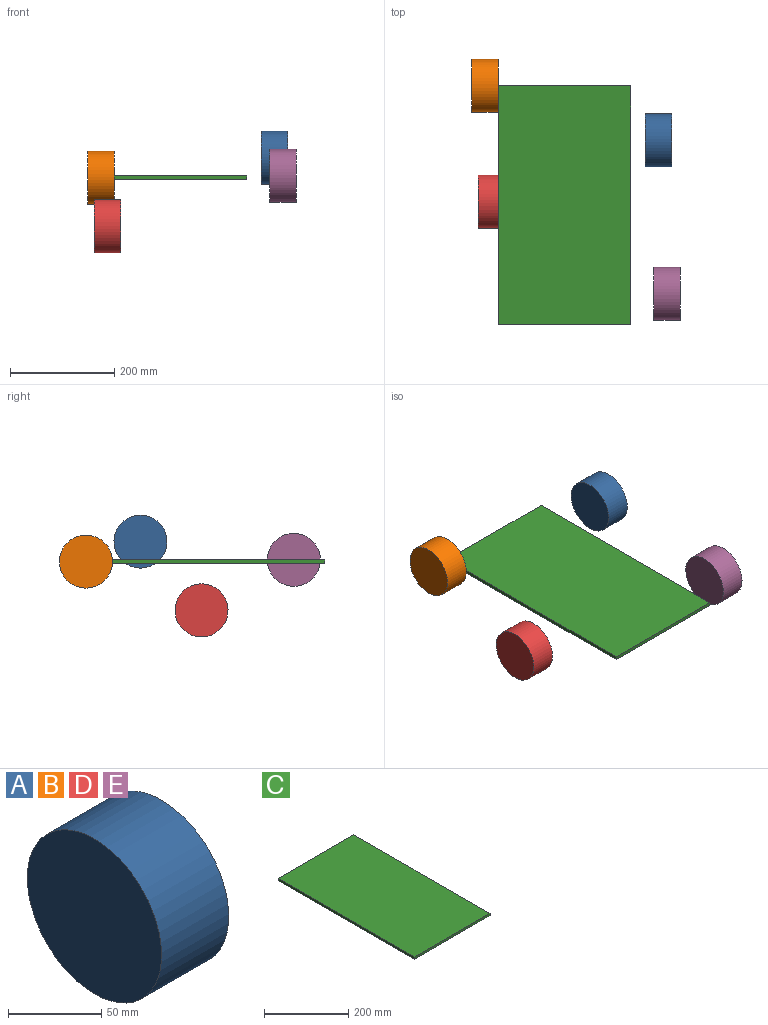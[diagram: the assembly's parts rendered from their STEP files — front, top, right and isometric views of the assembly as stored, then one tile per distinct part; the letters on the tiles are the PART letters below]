
ASSEMBLY  parts=5 mates=1
PART A: 3 faces, bbox 50.8x101.6x101.6 mm
  f0: cylinder r=50.8mm len=101.6mm, axis (-1,0,0), area 16214.6mm2, adj f1,f2
  f1: plane 101.6x101.6mm, normal (1,0,0), area 8107.3mm2, adj f0
  f2: plane 101.6x101.6mm, normal (-1,0,0), area 8107.3mm2, adj f0
PART B: same geometry as A
PART C: 6 faces, bbox 254x457.2x6.4 mm
  f0: plane 254x6.35mm, normal (0,-1,0), area 1612.9mm2, adj f1,f3,f4,f5
  f1: plane 457.2x6.35mm, normal (1,0,0), area 2903.2mm2, adj f0,f2,f4,f5
  f2: plane 254x6.35mm, normal (0,1,0), area 1612.9mm2, adj f1,f3,f4,f5
  f3: plane 457.2x6.35mm, normal (-1,0,0), area 2903.2mm2, adj f0,f2,f4,f5
  f4: plane 457.2x254mm, normal (0,0,1), area 116128.8mm2, adj f0,f1,f2,f3
  f5: plane 457.2x254mm, normal (0,0,-1), area 116128.8mm2, adj f0,f1,f2,f3
PART D: same geometry as A
PART E: same geometry as A
PLACE A t=(153.4,122.79,37.19)mm
PLACE B t=(-178.79,227.3,-1.09)mm
PLACE C t=(-0.99,-1.3,-4.27)mm
PLACE D t=(-166.43,5.86,-94.52)mm
PLACE E t=(170.14,-171.12,2.27)mm
MATE revolute B.f0 <-> C.f3  axis (1,0,0) through (-127.99,227.3,-1.09)mm
